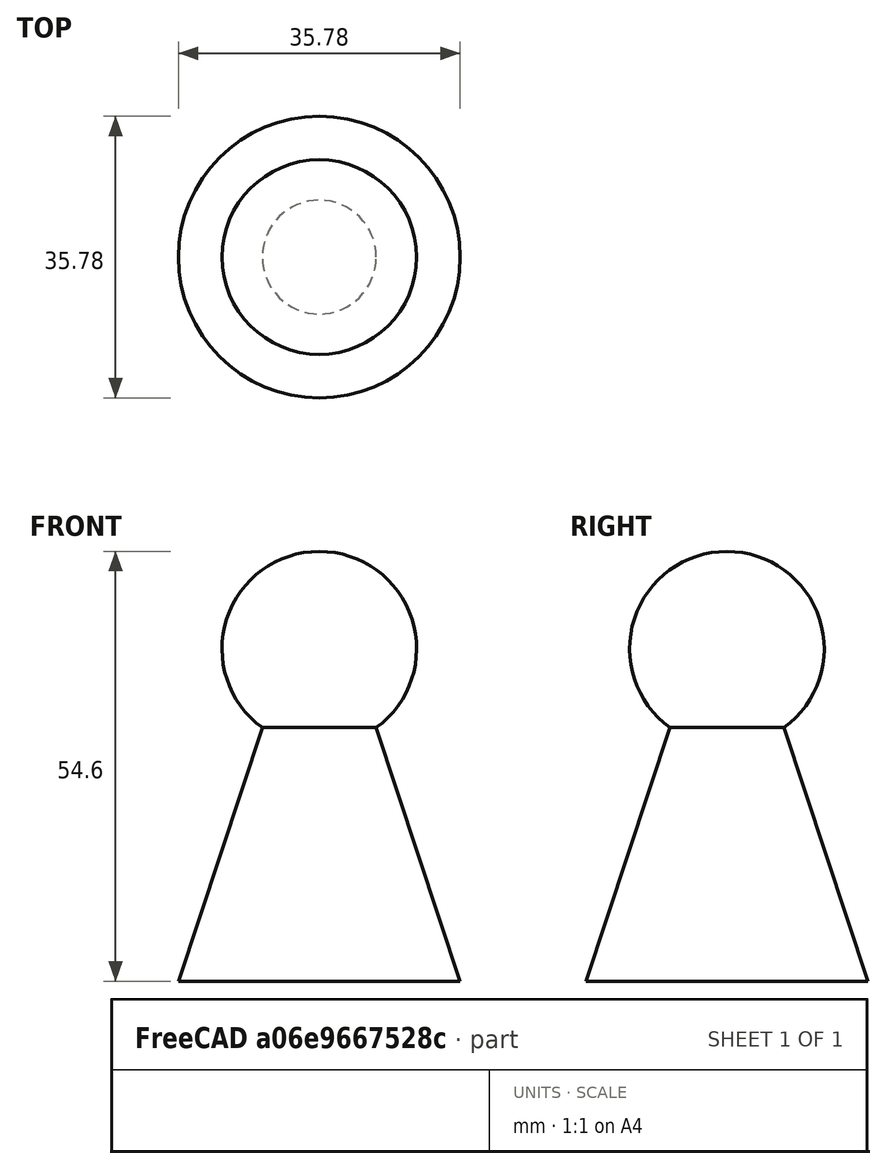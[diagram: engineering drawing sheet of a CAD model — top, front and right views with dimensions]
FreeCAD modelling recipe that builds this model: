
FCSTD DOCUMENT  (FreeCAD 0.16R6707 (Git))
Label: ficha
License: All rights reserved
LicenseURL: http://en.wikipedia.org/wiki/All_rights_reserved
objects: Sketcher::SketchObject×1, PartDesign::Revolution×1
note: 3 computed .brp shape members not serialized (recipe doc carries the construction recipe); baked Part::Feature solids carry a one-line shape summary decoded from their .brp

FEATURE [Sketcher::SketchObject] Sketch
  Placement = pos=(0,0,0) rot=(-1,0,0;4.71239rad)
  sketch-geometry (4):
    g0: ArcOfCircle CenterX=0 CenterY=42.2361 CenterZ=0 NormalX=0 NormalY=0 NormalZ=1 Radius=12.3609 StartAngle=5.33753 EndAngle=7.85398
    g1: LineSegment StartX=7.23378 StartY=32.2129 StartZ=0 EndX=17.895 EndY=0 EndZ=0
    g2: LineSegment StartX=17.895 StartY=0 StartZ=0 EndX=0 EndY=0 EndZ=0
    g3: LineSegment StartX=0 StartY=0 StartZ=0 EndX=0 EndY=54.5971 EndZ=0
  constraints (8):
    c: PointOnObject(g0,g-2)
    c: PointOnObject(g0,g-2)
    c: Coincident(g1,g0)
    c: PointOnObject(g1,g-1)
    c: Coincident(g1,g2)
    c: Coincident(g2,g-1)
    c: Coincident(g2,g3)
    c: Coincident(g3,g0)
FEATURE [PartDesign::Revolution] Revolution
  Angle = 360
  Axis = (0,0,1)
  Base = (0,0,0)
  Placement = pos=(0,0,0) rot=(-1,0,0;4.71239rad)
  ReferenceAxis = -> Sketch [V_Axis]
  Reversed = true
  Sketch = -> Sketch
